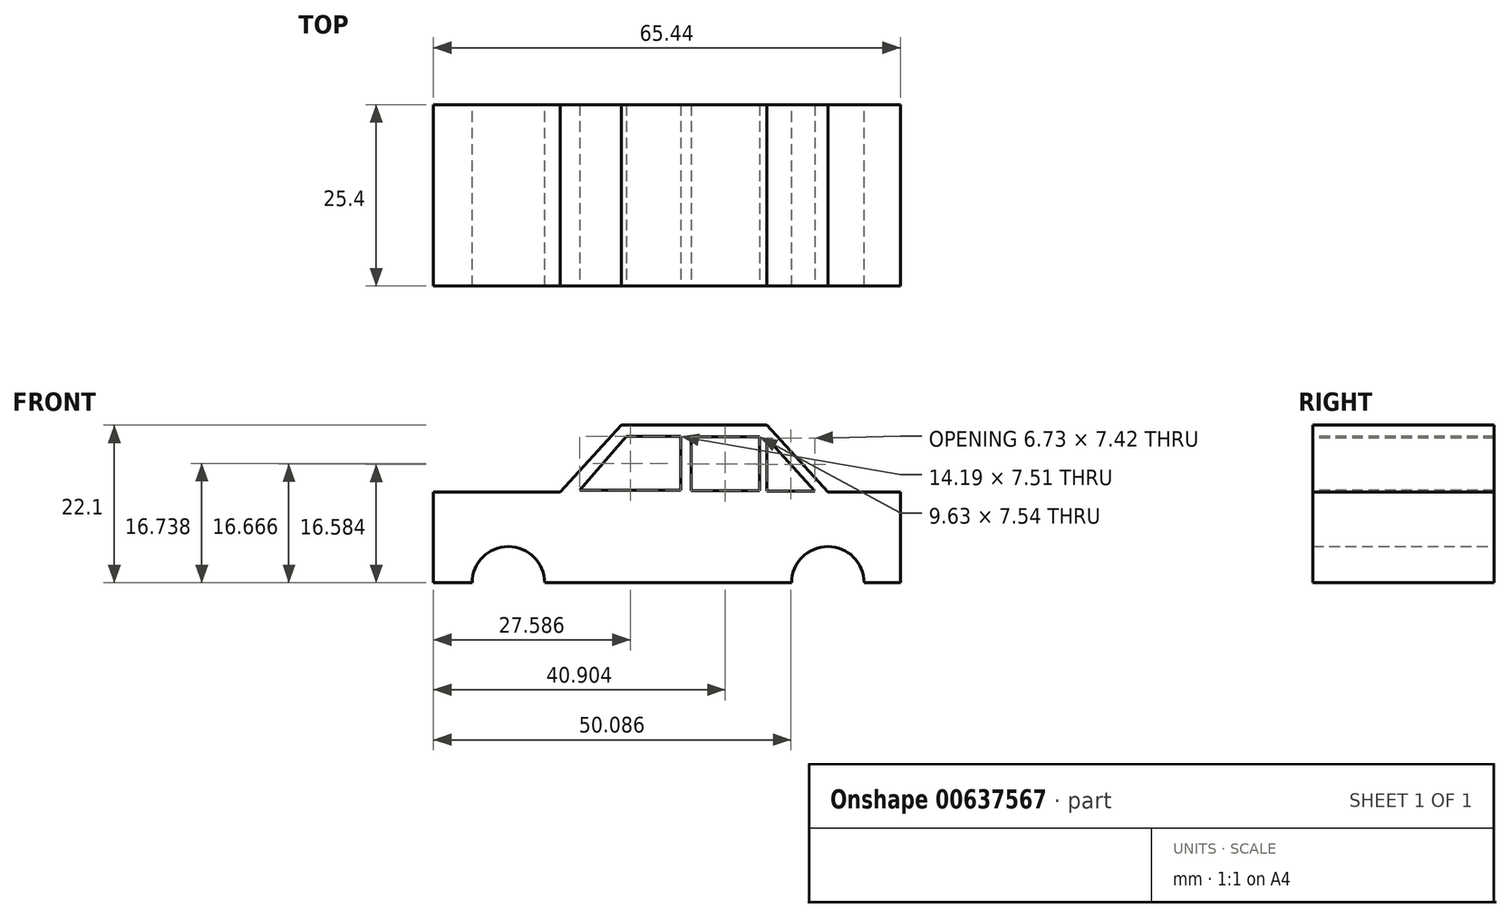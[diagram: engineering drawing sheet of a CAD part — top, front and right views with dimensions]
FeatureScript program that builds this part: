
annotation { "Feature Type Name" : "Feature", "Feature Type Description" : "" }
export const myFeature = defineFeature(function(context is Context, id is Id, definition is map)
    precondition{}
    {
        {
            var Q0;
            Q0=qCreatedBy(makeId("Front.planeOp"),FACE);
            var sketch = newSketch(context, id + "F0", { "sketchPlane" : qUnion([Q0])});
            skLineSegment(sketch, "E0", {"start": v(-55.28, 12.7) * mm, "end": v(-37.5, 12.7) * mm});
            skLineSegment(sketch, "E1", {"start": v(-37.5, 12.7) * mm, "end": v(-28.96, 22.1) * mm});
            skLineSegment(sketch, "E2", {"start": v(-28.96, 22.1) * mm, "end": v(-8.54, 22.1) * mm});
            skLineSegment(sketch, "E3", {"start": v(-8.54, 22.1) * mm, "end": v(0, 12.7) * mm});
            skLineSegment(sketch, "E4", {"start": v(0, 12.7) * mm, "end": v(10.16, 12.7) * mm});
            skLineSegment(sketch, "E5", {"start": v(10.16, 12.7) * mm, "end": v(10.16, 0) * mm});
            skLineSegment(sketch, "E6", {"start": v(-55.28, 12.7) * mm, "end": v(-55.28, 0) * mm});
            skLineSegment(sketch, "E7", {"start": v(-55.28, 0) * mm, "end": v(-49.86, 0) * mm});
            skArc(sketch, "E8", {"start": v(-39.7, 0) * mm, "mid": v(-44.78, 5.08) * mm, "end": v(-49.86, 0) * mm});
            skArc(sketch, "E9", {"start": v(5.08, 0) * mm, "mid": v(0, 5.08) * mm, "end": v(-5.08, 0) * mm});
            skLineSegment(sketch, "E10.trimOffspring", {"start": v(-39.7, 0) * mm, "end": v(-5.08, 0) * mm});
            skLineSegment(sketch, "E11.trimOffspring", {"start": v(5.08, 0) * mm, "end": v(10.16, 0) * mm});
            skSolve(sketch);
        }
        {
            var Q0;
            Q0 = qSketchRegion(id + "F0", true);
            extrude(context, id + "F1", {"entities" : qUnion([Q0]), "depth" : 25.4 * mm, "offsetDistance" : 25.4 * mm});
        }
        {
            var Q0;
            Q0=makeQuery(id+"F1.opExtrude","CAP_FACE",FACE,{"disambiguationData":[OSD([sQuery(id+"F0.wireOp",EDGE,"E0"),sQuery(id+"F0.wireOp",EDGE,"E1"),sQuery(id+"F0.wireOp",EDGE,"E2"),sQuery(id+"F0.wireOp",EDGE,"E3"),sQuery(id+"F0.wireOp",EDGE,"E4"),sQuery(id+"F0.wireOp",EDGE,"E5"),sQuery(id+"F0.wireOp",EDGE,"E6"),sQuery(id+"F0.wireOp",EDGE,"E7"),sQuery(id+"F0.wireOp",EDGE,"E8"),sQuery(id+"F0.wireOp",EDGE,"E9"),sQuery(id+"F0.wireOp",EDGE,"E10.trimOffspring"),sQuery(id+"F0.wireOp",EDGE,"E11.trimOffspring")])],"isStart":false});
            var sketch = newSketch(context, id + "F2", { "sketchPlane" : qUnion([Q0])});
            skLineSegment(sketch, "E12", {"start": v(-34.79, 12.98) * mm, "end": v(-28.25, 20.5) * mm});
            skLineSegment(sketch, "E13", {"start": v(-28.25, 20.5) * mm, "end": v(-20.6, 20.5) * mm});
            skLineSegment(sketch, "E14", {"start": v(-20.6, 20.5) * mm, "end": v(-20.6, 12.98) * mm});
            skLineSegment(sketch, "E15", {"start": v(-34.79, 12.98) * mm, "end": v(-20.6, 12.98) * mm});
            skPoint(sketch, "E16.orphan", {"position": v(-20.6, 12.41) * mm});
            skSolve(sketch);
        }
        {
            var Q0;
            Q0 = qSketchRegion(id + "F2", true);
            extrude(context, id + "F3", {"entities" : qUnion([Q0]), "operationType" : NewBodyOperationType.REMOVE, "oppositeDirection" : true, "depth" : 25.4 * mm, "offsetDistance" : 25.4 * mm});
        }
        {
            var Q0;
            Q0=makeQuery(id+"F1.opExtrude","CAP_FACE",FACE,{"disambiguationData":[OSD([sQuery(id+"F0.wireOp",EDGE,"E0"),sQuery(id+"F0.wireOp",EDGE,"E1"),sQuery(id+"F0.wireOp",EDGE,"E2"),sQuery(id+"F0.wireOp",EDGE,"E3"),sQuery(id+"F0.wireOp",EDGE,"E4"),sQuery(id+"F0.wireOp",EDGE,"E5"),sQuery(id+"F0.wireOp",EDGE,"E6"),sQuery(id+"F0.wireOp",EDGE,"E7"),sQuery(id+"F0.wireOp",EDGE,"E8"),sQuery(id+"F0.wireOp",EDGE,"E9"),sQuery(id+"F0.wireOp",EDGE,"E10.trimOffspring"),sQuery(id+"F0.wireOp",EDGE,"E11.trimOffspring")])],"isStart":false});
            var sketch = newSketch(context, id + "F4", { "sketchPlane" : qUnion([Q0])});
            skLineSegment(sketch, "E17.bottom", {"start": v(-19.2, 20.44) * mm, "end": v(-9.56, 20.44) * mm});
            skLineSegment(sketch, "E17.top", {"start": v(-19.2, 12.9) * mm, "end": v(-9.56, 12.9) * mm});
            skLineSegment(sketch, "E17.left", {"start": v(-19.2, 20.44) * mm, "end": v(-19.2, 12.9) * mm});
            skLineSegment(sketch, "E17.right", {"start": v(-9.56, 20.44) * mm, "end": v(-9.56, 12.9) * mm});
            skSolve(sketch);
        }
        {
            var Q0;
            Q0 = qSketchRegion(id + "F4", true);
            extrude(context, id + "F5", {"entities" : qUnion([Q0]), "operationType" : NewBodyOperationType.REMOVE, "oppositeDirection" : true, "depth" : 25.4 * mm, "offsetDistance" : 25.4 * mm});
        }
        {
            var Q0;
            Q0=makeQuery(id+"F1.opExtrude","CAP_FACE",FACE,{"disambiguationData":[OSD([sQuery(id+"F0.wireOp",EDGE,"E0"),sQuery(id+"F0.wireOp",EDGE,"E1"),sQuery(id+"F0.wireOp",EDGE,"E2"),sQuery(id+"F0.wireOp",EDGE,"E3"),sQuery(id+"F0.wireOp",EDGE,"E4"),sQuery(id+"F0.wireOp",EDGE,"E5"),sQuery(id+"F0.wireOp",EDGE,"E6"),sQuery(id+"F0.wireOp",EDGE,"E7"),sQuery(id+"F0.wireOp",EDGE,"E8"),sQuery(id+"F0.wireOp",EDGE,"E9"),sQuery(id+"F0.wireOp",EDGE,"E10.trimOffspring"),sQuery(id+"F0.wireOp",EDGE,"E11.trimOffspring")])],"isStart":false});
            var sketch = newSketch(context, id + "F6", { "sketchPlane" : qUnion([Q0])});
            skLineSegment(sketch, "E18", {"start": v(-8.56, 20.3) * mm, "end": v(-8.56, 12.87) * mm});
            skLineSegment(sketch, "E19", {"start": v(-8.56, 12.87) * mm, "end": v(-1.83, 12.87) * mm});
            skLineSegment(sketch, "E20", {"start": v(-1.83, 12.87) * mm, "end": v(-8.56, 20.3) * mm});
            skSolve(sketch);
        }
        {
            var Q0;
            Q0 = qSketchRegion(id + "F6", true);
            extrude(context, id + "F7", {"entities" : qUnion([Q0]), "operationType" : NewBodyOperationType.REMOVE, "oppositeDirection" : true, "depth" : 25.4 * mm, "offsetDistance" : 25.4 * mm});
        }
    });
